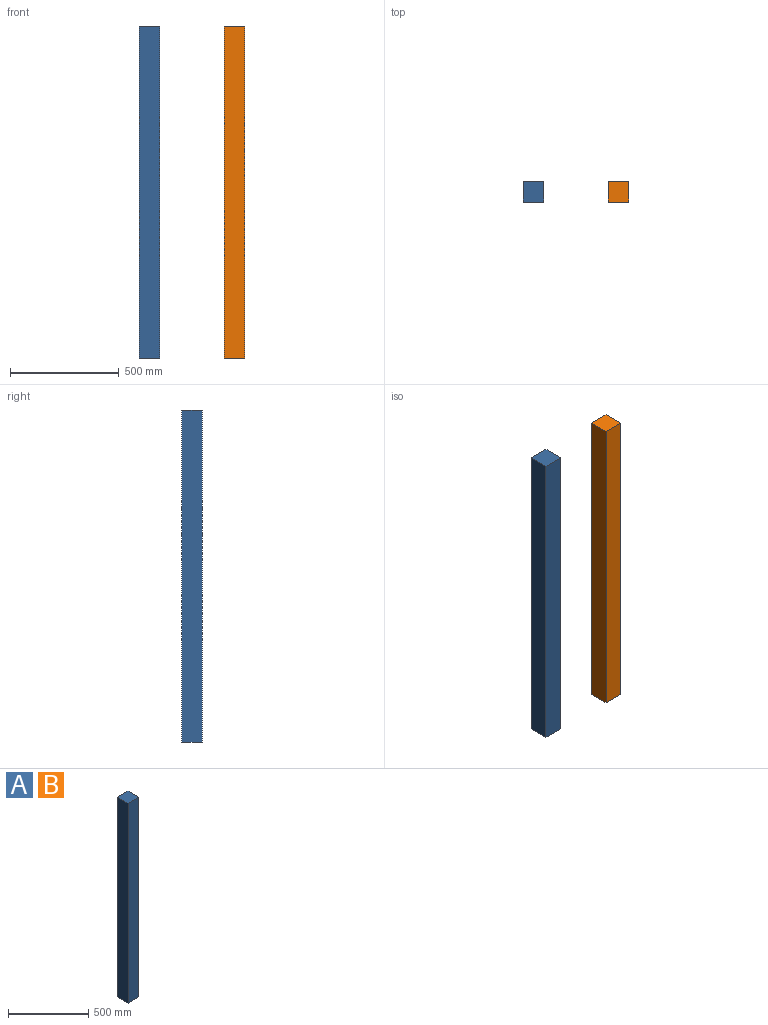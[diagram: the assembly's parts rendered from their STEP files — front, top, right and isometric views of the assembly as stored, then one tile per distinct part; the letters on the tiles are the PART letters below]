
ASSEMBLY  parts=2 mates=1
PART A: 6 faces, bbox 95.3x95.3x1524 mm
  f0: plane 1524x95.25mm, normal (1,0,0), area 145161mm2, adj f1,f3,f4,f5
  f1: plane 1524x95.25mm, normal (0,1,0), area 145161mm2, adj f0,f2,f4,f5
  f2: plane 1524x95.25mm, normal (-1,0,0), area 145161mm2, adj f1,f3,f4,f5
  f3: plane 1524x95.25mm, normal (0,-1,0), area 145161mm2, adj f0,f2,f4,f5
  f4: plane 95.25x95.25mm, normal (0,0,1), area 9072.6mm2, adj f0,f1,f2,f3
  f5: plane 95.25x95.25mm, normal (0,0,-1), area 9072.6mm2, adj f0,f1,f2,f3
PART B: same geometry as A
PLACE A t=(174.16,0,-81.07)mm
PLACE B t=(564.19,0,-81.07)mm
MATE parallel A.f3 <-> B.f3  axis (0,-1,0) through (174.31,-40.34,1442.93)mm
